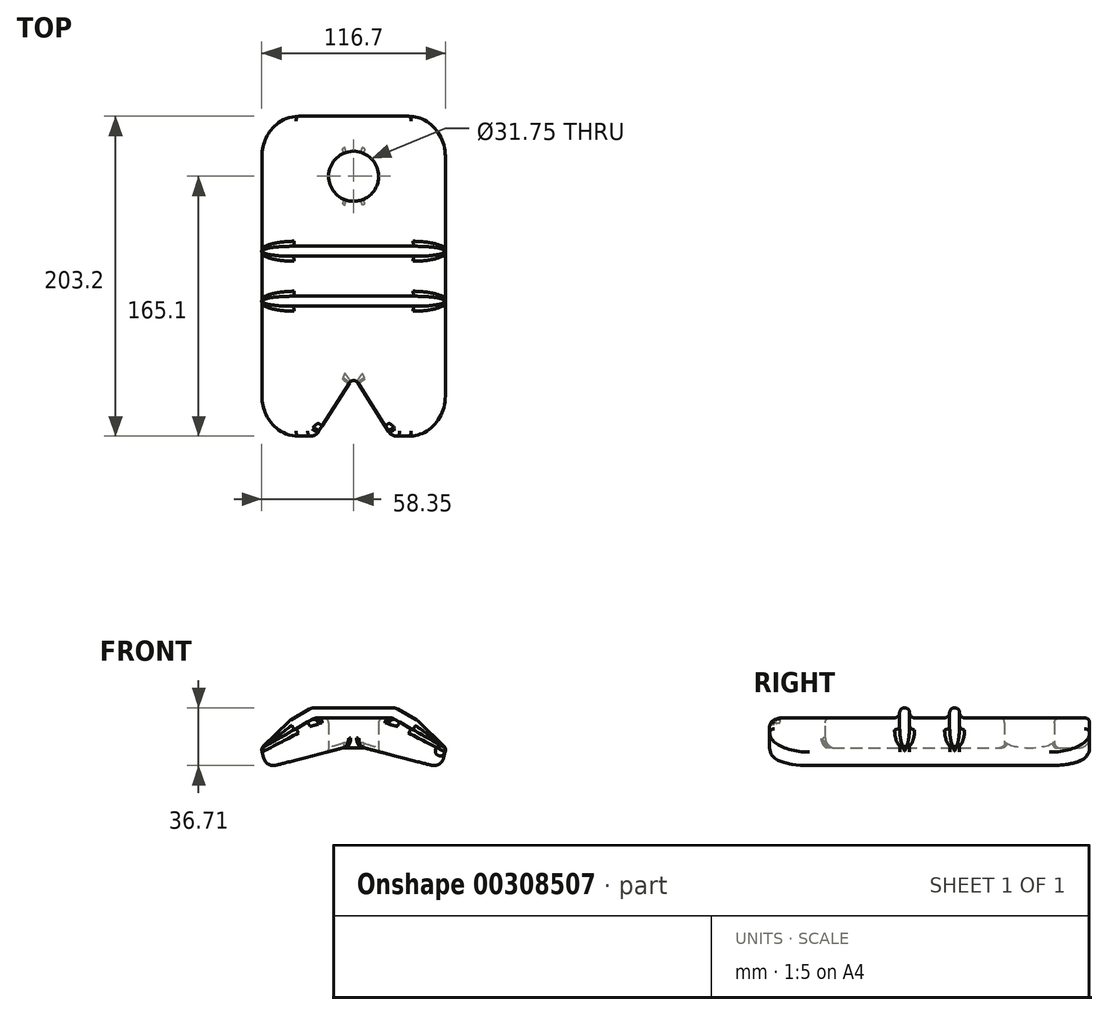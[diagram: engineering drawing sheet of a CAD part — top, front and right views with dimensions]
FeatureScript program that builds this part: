
annotation { "Feature Type Name" : "Feature", "Feature Type Description" : "" }
export const myFeature = defineFeature(function(context is Context, id is Id, definition is map)
    precondition{}
    {
        {
            var Q0;
            Q0=qCreatedBy(makeId("Front.planeOp"),FACE);
            var sketch = newSketch(context, id + "F0", { "sketchPlane" : qUnion([Q0])});
            skLineSegment(sketch, "E0", {"start": v(0, 0) * mm, "end": v(-6.35, 0) * mm});
            skLineSegment(sketch, "E1", {"start": v(-6.35, 0) * mm, "end": v(-55.54, -12.7) * mm});
            skLineSegment(sketch, "E2", {"start": v(-55.54, -12.7) * mm, "end": v(-58.71, -0.4) * mm});
            skLineSegment(sketch, "E3", {"start": v(-58.71, -0.4) * mm, "end": v(-24.3, 19.05) * mm});
            skLineSegment(sketch, "E4", {"start": v(-24.3, 19.05) * mm, "end": v(24.3, 19.05) * mm});
            skLineSegment(sketch, "E5", {"start": v(24.3, 19.05) * mm, "end": v(58.71, -0.4) * mm});
            skLineSegment(sketch, "E6", {"start": v(58.71, -0.4) * mm, "end": v(55.54, -12.7) * mm});
            skLineSegment(sketch, "E7", {"start": v(55.54, -12.7) * mm, "end": v(6.35, 0) * mm});
            skLineSegment(sketch, "E8", {"start": v(6.35, 0) * mm, "end": v(0, 0) * mm});
            skSolve(sketch);
        }
        {
            var Q0;
            Q0=makeQuery(id+"F0.imprint","IMPRINT",FACE,{"disambiguationData":[TD([[makeQuery(id+"F0.imprint","IMPRINT",EDGE,{"derivedFrom":sQuery(id+"F0.wireOp",EDGE,"E0")}),-1.0]])]});
            extrude(context, id + "F1", {"entities" : qUnion([Q0]), "depth" : 203.2 * mm});
        }
        {
            var Q0;
            Q0=qCreatedBy(makeId("Top.planeOp"),FACE);
            var sketch = newSketch(context, id + "F2", { "sketchPlane" : qUnion([Q0])});
            skCircle(sketch, "E9", {"center": v(0, -38.1) * mm, "radius": 15.88 * mm});
            skLineSegment(sketch, "E10", {"start": v(-38.1, -225.24) * mm, "end": v(0, -165.1) * mm});
            skLineSegment(sketch, "E11", {"start": v(0, -165.1) * mm, "end": v(38.1, -225.24) * mm});
            skLineSegment(sketch, "E12", {"start": v(38.1, -225.24) * mm, "end": v(-38.1, -225.24) * mm});
            skSolve(sketch);
        }
        {
            var Q0;
            Q0 = qSketchRegion(id + "F2", true);
            extrude(context, id + "F3", {"entities" : qUnion([Q0]), "operationType" : NewBodyOperationType.REMOVE, "depth" : 76.2 * mm, "hasSecondDirection" : true, "secondDirectionOppositeDirection" : true, "secondDirectionDepth" : 25.4 * mm});
        }
        {
            var Q0;
            Q0=qCreatedBy(makeId("Front.planeOp"),FACE);
            var sketch = newSketch(context, id + "F4", { "sketchPlane" : qUnion([Q0])});
            skLineSegment(sketch, "E13", {"start": v(-58.71, -0.4) * mm, "end": v(-40.59, 17.4) * mm});
            skLineSegment(sketch, "E14", {"start": v(-40.59, 17.4) * mm, "end": v(-26.42, 25.4) * mm});
            skLineSegment(sketch, "E15", {"start": v(-26.42, 25.4) * mm, "end": v(26.42, 25.4) * mm});
            skLineSegment(sketch, "E16", {"start": v(26.42, 25.4) * mm, "end": v(40.59, 17.4) * mm});
            skLineSegment(sketch, "E17", {"start": v(40.59, 17.4) * mm, "end": v(58.71, -0.4) * mm});
            skLineSegment(sketch, "E18", {"start": v(-58.71, -0.4) * mm, "end": v(-55.54, -12.7) * mm});
            skLineSegment(sketch, "E19", {"start": v(-55.54, -12.7) * mm, "end": v(-6.35, 0) * mm});
            skLineSegment(sketch, "E20", {"start": v(-6.35, 0) * mm, "end": v(0, 0) * mm});
            skLineSegment(sketch, "E21", {"start": v(0, 0) * mm, "end": v(6.35, 0) * mm});
            skLineSegment(sketch, "E22", {"start": v(6.35, 0) * mm, "end": v(55.54, -12.7) * mm});
            skLineSegment(sketch, "E23", {"start": v(55.54, -12.7) * mm, "end": v(58.71, -0.4) * mm});
            skSolve(sketch);
        }
        {
            var Q0;
            Q0 = qSketchRegion(id + "F4", true);
            extrude(context, id + "F5", {"entities" : qUnion([Q0]), "operationType" : NewBodyOperationType.ADD, "depth" : 88.9 * mm, "hasSecondDirection" : true, "secondDirectionOppositeDirection" : false, "secondDirectionDepth" : 82.55 * mm});
        }
        {
            var Q0;
            Q0 = qSketchRegion(id + "F4", true);
            extrude(context, id + "F6", {"entities" : qUnion([Q0]), "operationType" : NewBodyOperationType.ADD, "depth" : 120.65 * mm, "hasSecondDirection" : true, "secondDirectionOppositeDirection" : false, "secondDirectionDepth" : 114.3 * mm});
        }
        {
            var Q0;
            Q0=makeQuery(id+"F1.opExtrude","CAP_EDGE",EDGE,{"disambiguationData":[OSD([sQuery(id+"F0.wireOp",EDGE,"E2")])],"isStart":false});
            var Q1;
            Q1=makeQuery(id+"F1.opExtrude","CAP_EDGE",EDGE,{"disambiguationData":[OSD([sQuery(id+"F0.wireOp",EDGE,"E6")])],"isStart":false});
            var Q2;
            Q2=makeQuery(id+"F1.opExtrude","CAP_EDGE",EDGE,{"disambiguationData":[OSD([sQuery(id+"F0.wireOp",EDGE,"E6")])],"isStart":true});
            var Q3;
            Q3=makeQuery(id+"F1.opExtrude","CAP_EDGE",EDGE,{"disambiguationData":[OSD([sQuery(id+"F0.wireOp",EDGE,"E2")])],"isStart":true});
            fillet(context, id + "F7", {"entities" : qUnion([Q0, Q1, Q2, Q3]), "radius" : 25.4 * mm, "tangentPropagation" : true, "allowEdgeOverflow" : false});
        }
        {
            var Q0;
            {var subQ0=sQuery(id+"F0.wireOp",EDGE,"E4");var subQ1=sQuery(id+"F0.wireOp",EDGE,"E3");var subQ4=sQuery(id+"F4.wireOp",EDGE,"E17");var subQ5=sQuery(id+"F4.wireOp",EDGE,"E16");var subQ6=sQuery(id+"F4.wireOp",EDGE,"E15");var subQ7=sQuery(id+"F4.wireOp",EDGE,"E14");var subQ8=sQuery(id+"F4.wireOp",EDGE,"E13");var subQ9=sQuery(id+"F4.wireOp",EDGE,"00726857-9862-420c-8028-ea9e9dc75423");var subQ10=sQuery(id+"F4.wireOp",EDGE,"c4d77a14-dad9-4408-b2c3-eb6264689465");var subQ11=sQuery(id+"F4.wireOp",EDGE,"1c61bb94-5c36-4dd5-8af5-db9b8bca0218");Q0=makeQuery(id+"F6.boolean.opBoolean","SPLIT",EDGE,{"disambiguationData":[TD([makeQuery(id+"F6.opExtrude","CAP_FACE",FACE,{"disambiguationData":[OSD([subQ11,subQ10,subQ9,subQ8,subQ7,subQ6,subQ5,subQ4])],"isStart":false})])],"derivedFrom":makeQuery(id+"F5.boolean.opBoolean","SPLIT",EDGE,{"disambiguationData":[TD([makeQuery(id+"F5.opExtrude","CAP_FACE",FACE,{"disambiguationData":[OSD([subQ11,subQ10,subQ9,subQ8,subQ7,subQ6,subQ5,subQ4])],"isStart":false})])],"derivedFrom":makeQuery(id+"F1.opExtrude","SWEPT_EDGE",EDGE,{"disambiguationData":[OSD([subQ1,subQ0])]})})});}
            var Q1;
            {var subQ0=sQuery(id+"F0.wireOp",EDGE,"E3");var subQ2=sQuery(id+"F4.wireOp",EDGE,"E17");var subQ3=sQuery(id+"F4.wireOp",EDGE,"E16");var subQ4=sQuery(id+"F4.wireOp",EDGE,"E15");var subQ5=sQuery(id+"F4.wireOp",EDGE,"E14");var subQ6=sQuery(id+"F4.wireOp",EDGE,"E13");var subQ7=sQuery(id+"F4.wireOp",EDGE,"00726857-9862-420c-8028-ea9e9dc75423");var subQ8=sQuery(id+"F4.wireOp",EDGE,"c4d77a14-dad9-4408-b2c3-eb6264689465");var subQ9=sQuery(id+"F4.wireOp",EDGE,"1c61bb94-5c36-4dd5-8af5-db9b8bca0218");var subQ10=sQuery(id+"F0.wireOp",EDGE,"E4");var subQ12=makeQuery(id+"F5.opExtrude","CAP_FACE",FACE,{"disambiguationData":[OSD([subQ9,subQ8,subQ7,subQ6,subQ5,subQ4,subQ3,subQ2])],"isStart":false});Q1=makeQuery(id+"F6.boolean.opBoolean","SPLIT",EDGE,{"disambiguationData":[TD([subQ12])],"derivedFrom":makeQuery(id+"F5.boolean.opBoolean","SPLIT",EDGE,{"disambiguationData":[TD([subQ12])],"derivedFrom":makeQuery(id+"F1.opExtrude","SWEPT_EDGE",EDGE,{"disambiguationData":[OSD([subQ0,subQ10])]})})});}
            var Q2;
            Q2=makeQuery(id+"F6.opExtrude","SWEPT_EDGE",EDGE,{"disambiguationData":[OSD([sQuery(id+"F4.wireOp",EDGE,"E14"),sQuery(id+"F4.wireOp",EDGE,"E15")])]});
            var Q3;
            Q3=makeQuery(id+"F6.opExtrude","SWEPT_EDGE",EDGE,{"disambiguationData":[OSD([sQuery(id+"F4.wireOp",EDGE,"E13"),sQuery(id+"F4.wireOp",EDGE,"E14")])]});
            var Q4;
            Q4=makeQuery(id+"F5.opExtrude","SWEPT_EDGE",EDGE,{"disambiguationData":[OSD([sQuery(id+"F4.wireOp",EDGE,"E14"),sQuery(id+"F4.wireOp",EDGE,"E15")])]});
            var Q5;
            Q5=makeQuery(id+"F5.opExtrude","SWEPT_EDGE",EDGE,{"disambiguationData":[OSD([sQuery(id+"F4.wireOp",EDGE,"E13"),sQuery(id+"F4.wireOp",EDGE,"E14")])]});
            var Q6;
            {var subQ0=sQuery(id+"F0.wireOp",EDGE,"E5");var subQ1=sQuery(id+"F0.wireOp",EDGE,"E4");var subQ4=sQuery(id+"F4.wireOp",EDGE,"E17");var subQ5=sQuery(id+"F4.wireOp",EDGE,"E16");var subQ6=sQuery(id+"F4.wireOp",EDGE,"E15");var subQ7=sQuery(id+"F4.wireOp",EDGE,"E14");var subQ8=sQuery(id+"F4.wireOp",EDGE,"E13");var subQ9=sQuery(id+"F4.wireOp",EDGE,"00726857-9862-420c-8028-ea9e9dc75423");var subQ10=sQuery(id+"F4.wireOp",EDGE,"c4d77a14-dad9-4408-b2c3-eb6264689465");var subQ11=sQuery(id+"F4.wireOp",EDGE,"1c61bb94-5c36-4dd5-8af5-db9b8bca0218");Q6=makeQuery(id+"F6.boolean.opBoolean","SPLIT",EDGE,{"disambiguationData":[TD([makeQuery(id+"F6.opExtrude","CAP_FACE",FACE,{"disambiguationData":[OSD([subQ11,subQ10,subQ9,subQ8,subQ7,subQ6,subQ5,subQ4])],"isStart":false})])],"derivedFrom":makeQuery(id+"F5.boolean.opBoolean","SPLIT",EDGE,{"disambiguationData":[TD([makeQuery(id+"F5.opExtrude","CAP_FACE",FACE,{"disambiguationData":[OSD([subQ11,subQ10,subQ9,subQ8,subQ7,subQ6,subQ5,subQ4])],"isStart":false})])],"derivedFrom":makeQuery(id+"F1.opExtrude","SWEPT_EDGE",EDGE,{"disambiguationData":[OSD([subQ1,subQ0])]})})});}
            var Q7;
            {var subQ0=sQuery(id+"F0.wireOp",EDGE,"E4");var subQ2=sQuery(id+"F0.wireOp",EDGE,"E5");var subQ4=sQuery(id+"F4.wireOp",EDGE,"E17");var subQ5=sQuery(id+"F4.wireOp",EDGE,"E16");var subQ6=sQuery(id+"F4.wireOp",EDGE,"E15");var subQ7=sQuery(id+"F4.wireOp",EDGE,"E14");var subQ8=sQuery(id+"F4.wireOp",EDGE,"E13");var subQ9=sQuery(id+"F4.wireOp",EDGE,"00726857-9862-420c-8028-ea9e9dc75423");var subQ10=sQuery(id+"F4.wireOp",EDGE,"c4d77a14-dad9-4408-b2c3-eb6264689465");var subQ11=sQuery(id+"F4.wireOp",EDGE,"1c61bb94-5c36-4dd5-8af5-db9b8bca0218");var subQ12=makeQuery(id+"F5.opExtrude","CAP_FACE",FACE,{"disambiguationData":[OSD([subQ11,subQ10,subQ9,subQ8,subQ7,subQ6,subQ5,subQ4])],"isStart":false});Q7=makeQuery(id+"F6.boolean.opBoolean","SPLIT",EDGE,{"disambiguationData":[TD([subQ12])],"derivedFrom":makeQuery(id+"F5.boolean.opBoolean","SPLIT",EDGE,{"disambiguationData":[TD([subQ12])],"derivedFrom":makeQuery(id+"F1.opExtrude","SWEPT_EDGE",EDGE,{"disambiguationData":[OSD([subQ0,subQ2])]})})});}
            var Q8;
            {var subQ0=sQuery(id+"F0.wireOp",EDGE,"E5");var subQ1=sQuery(id+"F0.wireOp",EDGE,"E4");Q8=makeQuery(id+"F5.boolean.opBoolean","SPLIT",EDGE,{"disambiguationData":[TD([makeQuery(id+"F5.opExtrude","CAP_FACE",FACE,{"disambiguationData":[OSD([sQuery(id+"F4.wireOp",EDGE,"1c61bb94-5c36-4dd5-8af5-db9b8bca0218"),sQuery(id+"F4.wireOp",EDGE,"c4d77a14-dad9-4408-b2c3-eb6264689465"),sQuery(id+"F4.wireOp",EDGE,"00726857-9862-420c-8028-ea9e9dc75423"),sQuery(id+"F4.wireOp",EDGE,"E13"),sQuery(id+"F4.wireOp",EDGE,"E14"),sQuery(id+"F4.wireOp",EDGE,"E15"),sQuery(id+"F4.wireOp",EDGE,"E16"),sQuery(id+"F4.wireOp",EDGE,"E17")])],"isStart":true})])],"derivedFrom":makeQuery(id+"F1.opExtrude","SWEPT_EDGE",EDGE,{"disambiguationData":[OSD([subQ1,subQ0])]})});}
            var Q9;
            {var subQ0=sQuery(id+"F0.wireOp",EDGE,"E4");var subQ1=sQuery(id+"F0.wireOp",EDGE,"E3");Q9=makeQuery(id+"F5.boolean.opBoolean","SPLIT",EDGE,{"disambiguationData":[TD([makeQuery(id+"F5.opExtrude","CAP_FACE",FACE,{"disambiguationData":[OSD([sQuery(id+"F4.wireOp",EDGE,"1c61bb94-5c36-4dd5-8af5-db9b8bca0218"),sQuery(id+"F4.wireOp",EDGE,"c4d77a14-dad9-4408-b2c3-eb6264689465"),sQuery(id+"F4.wireOp",EDGE,"00726857-9862-420c-8028-ea9e9dc75423"),sQuery(id+"F4.wireOp",EDGE,"E13"),sQuery(id+"F4.wireOp",EDGE,"E14"),sQuery(id+"F4.wireOp",EDGE,"E15"),sQuery(id+"F4.wireOp",EDGE,"E16"),sQuery(id+"F4.wireOp",EDGE,"E17")])],"isStart":true})])],"derivedFrom":makeQuery(id+"F1.opExtrude","SWEPT_EDGE",EDGE,{"disambiguationData":[OSD([subQ1,subQ0])]})});}
            var Q10;
            Q10=makeQuery(id+"F6.opExtrude","SWEPT_EDGE",EDGE,{"disambiguationData":[OSD([sQuery(id+"F4.wireOp",EDGE,"E15"),sQuery(id+"F4.wireOp",EDGE,"E16")])]});
            var Q11;
            Q11=makeQuery(id+"F5.opExtrude","SWEPT_EDGE",EDGE,{"disambiguationData":[OSD([sQuery(id+"F4.wireOp",EDGE,"E15"),sQuery(id+"F4.wireOp",EDGE,"E16")])]});
            var Q12;
            Q12=makeQuery(id+"F5.opExtrude","SWEPT_EDGE",EDGE,{"disambiguationData":[OSD([sQuery(id+"F4.wireOp",EDGE,"E16"),sQuery(id+"F4.wireOp",EDGE,"E17")])]});
            var Q13;
            Q13=makeQuery(id+"F6.opExtrude","SWEPT_EDGE",EDGE,{"disambiguationData":[OSD([sQuery(id+"F4.wireOp",EDGE,"E16"),sQuery(id+"F4.wireOp",EDGE,"E17")])]});
            var Q14;
            {var subQ0=sQuery(id+"F0.wireOp",EDGE,"E8");var subQ1=sQuery(id+"F0.wireOp",EDGE,"E7");Q14=makeQuery(id+"F3.boolean.opBoolean","SPLIT",EDGE,{"disambiguationData":[TD([makeQuery(id+"F3.opExtrude","SWEPT_FACE",FACE,{"disambiguationData":[OSD([sQuery(id+"F2.wireOp",EDGE,"E11")])]})])],"derivedFrom":makeQuery(id+"F1.opExtrude","SWEPT_EDGE",EDGE,{"disambiguationData":[OSD([subQ1,subQ0])]})});}
            var Q15;
            {var subQ0=sQuery(id+"F0.wireOp",EDGE,"E0");var subQ1=sQuery(id+"F0.wireOp",EDGE,"E1");Q15=makeQuery(id+"F3.boolean.opBoolean","SPLIT",EDGE,{"disambiguationData":[TD([makeQuery(id+"F3.opExtrude","SWEPT_FACE",FACE,{"disambiguationData":[OSD([sQuery(id+"F2.wireOp",EDGE,"E10")])]})])],"derivedFrom":makeQuery(id+"F1.opExtrude","SWEPT_EDGE",EDGE,{"disambiguationData":[OSD([subQ0,subQ1])]})});}
            var Q16;
            {var subQ0=sQuery(id+"F0.wireOp",EDGE,"E8");var subQ1=sQuery(id+"F0.wireOp",EDGE,"E7");var subQ2=sQuery(id+"F0.wireOp",EDGE,"E0");Q16=makeQuery(id+"F3.boolean.opBoolean","SPLIT",EDGE,{"disambiguationData":[TD([makeQuery(id+"F1.opExtrude","CAP_FACE",FACE,{"disambiguationData":[OSD([subQ2,sQuery(id+"F0.wireOp",EDGE,"E1"),sQuery(id+"F0.wireOp",EDGE,"E2"),sQuery(id+"F0.wireOp",EDGE,"E3"),sQuery(id+"F0.wireOp",EDGE,"E4"),sQuery(id+"F0.wireOp",EDGE,"E5"),sQuery(id+"F0.wireOp",EDGE,"E6"),subQ1,subQ0])],"isStart":true})])],"derivedFrom":makeQuery(id+"F1.opExtrude","SWEPT_EDGE",EDGE,{"disambiguationData":[OSD([subQ1,subQ0])]})});}
            var Q17;
            {var subQ0=sQuery(id+"F0.wireOp",EDGE,"E8");var subQ1=sQuery(id+"F0.wireOp",EDGE,"E1");var subQ2=sQuery(id+"F0.wireOp",EDGE,"E0");Q17=makeQuery(id+"F3.boolean.opBoolean","SPLIT",EDGE,{"disambiguationData":[TD([makeQuery(id+"F1.opExtrude","CAP_FACE",FACE,{"disambiguationData":[OSD([subQ2,subQ1,sQuery(id+"F0.wireOp",EDGE,"E2"),sQuery(id+"F0.wireOp",EDGE,"E3"),sQuery(id+"F0.wireOp",EDGE,"E4"),sQuery(id+"F0.wireOp",EDGE,"E5"),sQuery(id+"F0.wireOp",EDGE,"E6"),sQuery(id+"F0.wireOp",EDGE,"E7"),subQ0])],"isStart":true})])],"derivedFrom":makeQuery(id+"F1.opExtrude","SWEPT_EDGE",EDGE,{"disambiguationData":[OSD([subQ2,subQ1])]})});}
            var Q18;
            Q18=makeQuery(id+"F3.boolean.opBoolean","INTERSECT",EDGE,{"derivedFrom":[makeQuery(id+"F1.opExtrude","CAP_FACE",FACE,{"disambiguationData":[OSD([sQuery(id+"F0.wireOp",EDGE,"E0"),sQuery(id+"F0.wireOp",EDGE,"E1"),sQuery(id+"F0.wireOp",EDGE,"E2"),sQuery(id+"F0.wireOp",EDGE,"E3"),sQuery(id+"F0.wireOp",EDGE,"E4"),sQuery(id+"F0.wireOp",EDGE,"E5"),sQuery(id+"F0.wireOp",EDGE,"E6"),sQuery(id+"F0.wireOp",EDGE,"E7"),sQuery(id+"F0.wireOp",EDGE,"E8")])],"isStart":false}),makeQuery(id+"F3.opExtrude","SWEPT_FACE",FACE,{"disambiguationData":[OSD([sQuery(id+"F2.wireOp",EDGE,"E10")])]})]});
            var Q19;
            Q19=makeQuery(id+"F3.boolean.opBoolean","INTERSECT",EDGE,{"derivedFrom":[makeQuery(id+"F1.opExtrude","CAP_FACE",FACE,{"disambiguationData":[OSD([sQuery(id+"F0.wireOp",EDGE,"E0"),sQuery(id+"F0.wireOp",EDGE,"E1"),sQuery(id+"F0.wireOp",EDGE,"E2"),sQuery(id+"F0.wireOp",EDGE,"E3"),sQuery(id+"F0.wireOp",EDGE,"E4"),sQuery(id+"F0.wireOp",EDGE,"E5"),sQuery(id+"F0.wireOp",EDGE,"E6"),sQuery(id+"F0.wireOp",EDGE,"E7"),sQuery(id+"F0.wireOp",EDGE,"E8")])],"isStart":false}),makeQuery(id+"F3.opExtrude","SWEPT_FACE",FACE,{"disambiguationData":[OSD([sQuery(id+"F2.wireOp",EDGE,"E11")])]})]});
            fillet(context, id + "F8", {"entities" : qUnion([Q0, Q1, Q2, Q3, Q4, Q5, Q6, Q7, Q8, Q9, Q10, Q11, Q12, Q13, Q14, Q15, Q16, Q17, Q18, Q19]), "radius" : 6.35 * mm, "tangentPropagation" : true, "allowEdgeOverflow" : false});
        }
        {
            var Q0;
            Q0=makeQuery(id+"F3.boolean.opBoolean","COPY",EDGE,{"derivedFrom":makeQuery(id+"F3.opExtrude","SWEPT_EDGE",EDGE,{"disambiguationData":[OSD([sQuery(id+"F2.wireOp",EDGE,"E10"),sQuery(id+"F2.wireOp",EDGE,"E11")])]})});
            var Q1;
            Q1=makeQuery(id+"F3.boolean.opBoolean","INTERSECT",EDGE,{"disambiguationData":[OD(0.0)],"derivedFrom":[makeQuery(id+"F1.opExtrude","SWEPT_FACE",FACE,{"disambiguationData":[OSD([sQuery(id+"F0.wireOp",EDGE,"E0"),sQuery(id+"F0.wireOp",EDGE,"E8")])]}),makeQuery(id+"F3.opExtrude","SWEPT_FACE",FACE,{"disambiguationData":[OSD([sQuery(id+"F2.wireOp",EDGE,"E9")])]})]});
            var Q2;
            Q2=makeQuery(id+"F3.boolean.opBoolean","INTERSECT",EDGE,{"derivedFrom":[makeQuery(id+"F1.opExtrude","SWEPT_FACE",FACE,{"disambiguationData":[OSD([sQuery(id+"F0.wireOp",EDGE,"E4")])]}),makeQuery(id+"F3.opExtrude","SWEPT_FACE",FACE,{"disambiguationData":[OSD([sQuery(id+"F2.wireOp",EDGE,"E9")])]})]});
            var Q3;
            Q3=makeQuery(id+"F5.opExtrude","CAP_EDGE",EDGE,{"disambiguationData":[OSD([sQuery(id+"F4.wireOp",EDGE,"E13")])],"isStart":false});
            var Q4;
            Q4=makeQuery(id+"F5.opExtrude","CAP_EDGE",EDGE,{"disambiguationData":[OSD([sQuery(id+"F4.wireOp",EDGE,"E13")])],"isStart":true});
            var Q5;
            Q5=makeQuery(id+"F6.opExtrude","CAP_EDGE",EDGE,{"disambiguationData":[OSD([sQuery(id+"F4.wireOp",EDGE,"E13")])],"isStart":true});
            var Q6;
            Q6=makeQuery(id+"F6.opExtrude","CAP_EDGE",EDGE,{"disambiguationData":[OSD([sQuery(id+"F4.wireOp",EDGE,"E13")])],"isStart":false});
            fillet(context, id + "F9", {"entities" : qUnion([Q0, Q1, Q2, Q3, Q4, Q5, Q6]), "radius" : 3.17 * mm, "tangentPropagation" : true, "allowEdgeOverflow" : false});
        }
        {
            var Q0;
            Q0=makeQuery(id+"F5.boolean.opBoolean","INTERSECT",EDGE,{"derivedFrom":[makeQuery(id+"F1.opExtrude","SWEPT_FACE",FACE,{"disambiguationData":[OSD([sQuery(id+"F0.wireOp",EDGE,"E4")])]}),makeQuery(id+"F5.opExtrude","CAP_FACE",FACE,{"disambiguationData":[OSD([sQuery(id+"F4.wireOp",EDGE,"E13"),sQuery(id+"F4.wireOp",EDGE,"E14"),sQuery(id+"F4.wireOp",EDGE,"E15"),sQuery(id+"F4.wireOp",EDGE,"E16"),sQuery(id+"F4.wireOp",EDGE,"E17"),sQuery(id+"F4.wireOp",EDGE,"E18"),sQuery(id+"F4.wireOp",EDGE,"E19"),sQuery(id+"F4.wireOp",EDGE,"E20"),sQuery(id+"F4.wireOp",EDGE,"E21"),sQuery(id+"F4.wireOp",EDGE,"E22"),sQuery(id+"F4.wireOp",EDGE,"E23")])],"isStart":false})]});
            var Q1;
            {var subQ0=sQuery(id+"F4.wireOp",EDGE,"E23");var subQ1=sQuery(id+"F4.wireOp",EDGE,"E22");var subQ2=sQuery(id+"F4.wireOp",EDGE,"E21");var subQ3=sQuery(id+"F4.wireOp",EDGE,"E20");var subQ4=sQuery(id+"F4.wireOp",EDGE,"E19");var subQ5=sQuery(id+"F4.wireOp",EDGE,"E18");var subQ6=sQuery(id+"F4.wireOp",EDGE,"E17");var subQ7=sQuery(id+"F4.wireOp",EDGE,"E16");var subQ8=sQuery(id+"F4.wireOp",EDGE,"E15");var subQ9=sQuery(id+"F4.wireOp",EDGE,"E14");var subQ10=sQuery(id+"F4.wireOp",EDGE,"E13");var subQ13=sQuery(id+"F0.wireOp",EDGE,"E4");Q1=makeQuery(id+"F6.boolean.opBoolean","INTERSECT",EDGE,{"derivedFrom":[makeQuery(id+"F5.boolean.opBoolean","SPLIT",FACE,{"disambiguationData":[TD([makeQuery(id+"F3.boolean.opBoolean","COPY",FACE,{"derivedFrom":makeQuery(id+"F3.opExtrude","SWEPT_FACE",FACE,{"disambiguationData":[OSD([sQuery(id+"F2.wireOp",EDGE,"E10")])]})})])],"derivedFrom":makeQuery(id+"F1.opExtrude","SWEPT_FACE",FACE,{"disambiguationData":[OSD([subQ13])]})}),makeQuery(id+"F6.opExtrude","CAP_FACE",FACE,{"disambiguationData":[OSD([subQ10,subQ9,subQ8,subQ7,subQ6,subQ5,subQ4,subQ3,subQ2,subQ1,subQ0])],"isStart":true})]});}
            fillet(context, id + "F10", {"entities" : qUnion([Q0, Q1]), "radius" : 3.17 * mm, "tangentPropagation" : true, "allowEdgeOverflow" : false});
        }
        {
            var Q0;
            Q0=makeQuery(id+"F1.opExtrude","SWEPT_EDGE",EDGE,{"disambiguationData":[OSD([sQuery(id+"F0.wireOp",EDGE,"E1"),sQuery(id+"F0.wireOp",EDGE,"E2")])]});
            fillet(context, id + "F11", {"entities" : qUnion([Q0]), "radius" : 6.35 * mm, "tangentPropagation" : true, "allowEdgeOverflow" : false});
        }
        {
            var Q0;
            {var subQ1=sQuery(id+"F0.wireOp",EDGE,"E2");var subQ3=sQuery(id+"F0.wireOp",EDGE,"E4");var subQ5=sQuery(id+"F0.wireOp",EDGE,"E3");var subQ6=makeQuery(id+"F1.opExtrude","CAP_FACE",FACE,{"disambiguationData":[OSD([sQuery(id+"F0.wireOp",EDGE,"E0"),sQuery(id+"F0.wireOp",EDGE,"E1"),subQ1,subQ5,subQ3,sQuery(id+"F0.wireOp",EDGE,"E5"),sQuery(id+"F0.wireOp",EDGE,"E6"),sQuery(id+"F0.wireOp",EDGE,"E7"),sQuery(id+"F0.wireOp",EDGE,"E8")])],"isStart":false});Q0=makeQuery(id+"F7.opFillet","BLEND_EDGE",EDGE,{"blendedFrom":[makeQuery(id+"F1.opExtrude","CAP_EDGE",EDGE,{"disambiguationData":[OSD([subQ1])],"isStart":false}),makeQuery(id+"F6.boolean.opBoolean","SPLIT",FACE,{"disambiguationData":[TD([subQ6])],"derivedFrom":makeQuery(id+"F5.boolean.opBoolean","SPLIT",FACE,{"disambiguationData":[TD([subQ6])],"derivedFrom":makeQuery(id+"F1.opExtrude","SWEPT_FACE",FACE,{"disambiguationData":[OSD([subQ5])]})})})],"blendedInto":[makeQuery(id+"F6.boolean.opBoolean","SPLIT",FACE,{"disambiguationData":[TD([subQ6])],"derivedFrom":makeQuery(id+"F5.boolean.opBoolean","SPLIT",FACE,{"disambiguationData":[TD([subQ6])],"derivedFrom":makeQuery(id+"F1.opExtrude","SWEPT_FACE",FACE,{"disambiguationData":[OSD([subQ5])]})})})]});}
            fillet(context, id + "F12", {"entities" : qUnion([Q0]), "radius" : 3.17 * mm, "tangentPropagation" : true, "allowEdgeOverflow" : false});
        }
    });
